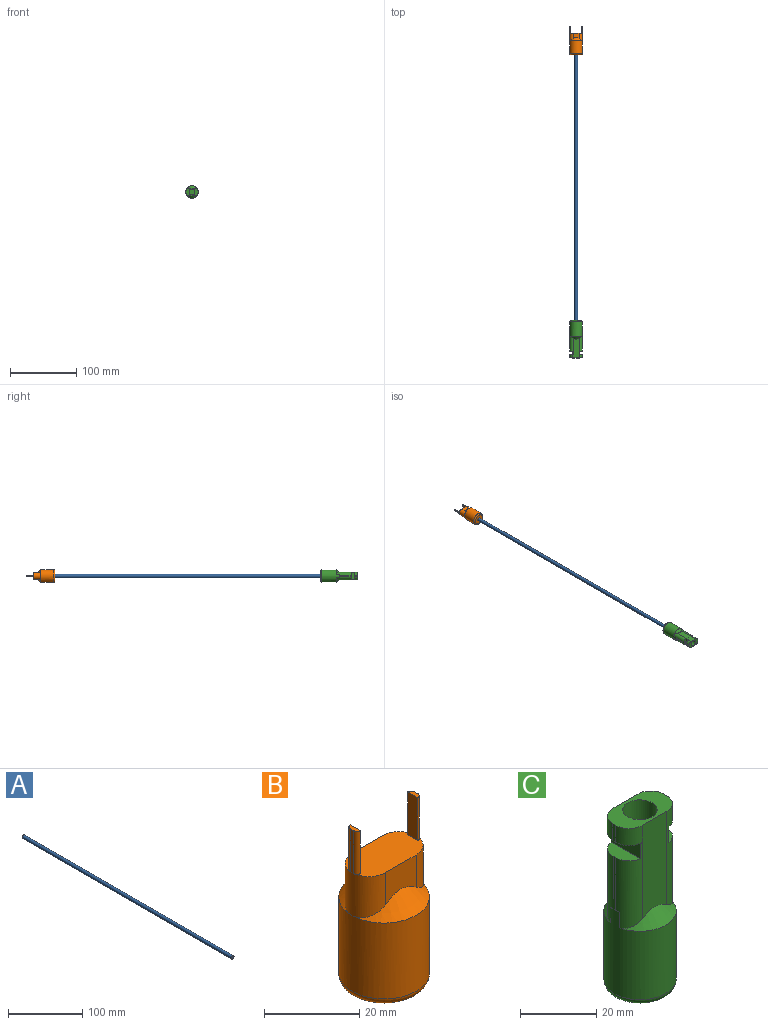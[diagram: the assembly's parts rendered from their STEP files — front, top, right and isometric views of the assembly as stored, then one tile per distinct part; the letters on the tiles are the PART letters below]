
ASSEMBLY  parts=3 mates=2
PART A: 3 faces, bbox 5x400x5 mm
  f0: cylinder r=2.5mm len=400mm, axis (0,1,0), area 6283.2mm2, adj f1,f2
  f1: plane 5x5mm, normal (0,-1,0), area 19.6mm2, adj f0
  f2: plane 5x5mm, normal (0,1,0), area 19.6mm2, adj f0
PART B: 24 faces, bbox 20.6x20.6x43.5 mm
  f0: plane 18.84x10mm, normal (0,0,1), area 163.5mm2, adj f5,f6,f7,f8,f13,f17,f19,f20
  f1: cone r=4.5mm half-angle=45deg, axis (0,0,-1), area 81.3mm2, adj f3,f6,f7,f8
  f2: plane 15x15mm, normal (0,0,-1), area 176.7mm2, adj f23
  f3: cylinder r=9.5mm len=19.5mm, axis (0,0,1), area 1164mm2, adj f1,f4,f23
  f4: cone r=4.5mm half-angle=45deg, axis (0,0,-1), area 81.3mm2, adj f3,f5,f7,f8
  f5: plane 9.01x8.23mm, normal (0,-1,0), area 64mm2, adj f0,f4,f7,f8
  f6: plane 9.01x8.23mm, normal (0,1,0), area 64mm2, adj f0,f1,f7,f8
  f7: cylinder r=5mm len=11mm, axis (0,0,1), area 158mm2, adj f0,f1,f4,f5,f6,f14,f15
  f8: cylinder r=5mm len=11mm, axis (0,0,-1), area 158mm2, adj f0,f1,f4,f5,f6,f9,f10
  f9: plane 0.89x0.08mm, normal (0,0,-1), area 0mm2, adj f8,f11,f20
  f10: plane 0.89x0.08mm, normal (0,0,-1), area 0mm2, adj f8,f11,f19
  f11: plane 11x1mm, normal (1,0,0), area 11mm2, adj f9,f10,f12,f19,f20
  f12: plane 3x1mm, normal (0,0,1), area 2.6mm2, adj f11,f13,f19,f20
  f13: plane 11x3mm, normal (-1,0,0), area 33mm2, adj f0,f12,f19,f20
  f14: plane 0.89x0.08mm, normal (0,0,-1), area 0mm2, adj f7,f16,f21
  f15: plane 0.89x0.08mm, normal (0,0,-1), area 0mm2, adj f7,f16,f22
  f16: plane 11x1mm, normal (-1,0,0), area 11mm2, adj f14,f15,f18,f21,f22
  f17: plane 11x3mm, normal (1,0,0), area 33mm2, adj f0,f18,f21,f22
  f18: plane 3x1mm, normal (0,0,1), area 2.6mm2, adj f16,f17,f21,f22
  f19: cylinder r=1mm len=11mm, axis (0,0,1), area 17.3mm2, adj f0,f10,f11,f12,f13
  f20: cylinder r=1mm len=11mm, axis (0,0,-1), area 17.3mm2, adj f0,f9,f11,f12,f13
  f21: cylinder r=1mm len=11mm, axis (0,0,-1), area 17.3mm2, adj f0,f14,f16,f17,f18
  f22: cylinder r=1mm len=11mm, axis (0,0,1), area 17.3mm2, adj f0,f15,f16,f17,f18
  f23: torus R=7.5mm, axis (0,0,1), area 173.2mm2, adj f2,f3
PART C: 30 faces, bbox 20.6x20.6x56.5 mm
  f0: cylinder r=9.5mm len=27.03mm, axis (0,0,1), area 1351.2mm2, adj f2,f3,f4,f5,f19,f20,f21,f22
  f1: plane 15x15mm, normal (0,0,-1), area 176.7mm2, adj f29
  f2: plane 1.8x0.17mm, normal (0,0,-1), area 0mm2, adj f0,f9,f21
  f3: plane 1.8x0.17mm, normal (0,0,-1), area 0mm2, adj f0,f9,f23
  f4: plane 1.8x0.17mm, normal (0,0,-1), area 0mm2, adj f0,f8,f22
  f5: plane 1.8x0.17mm, normal (0,0,-1), area 0mm2, adj f0,f8,f24
  f6: plane 10.87x5mm, normal (-1,0,0), area 54.4mm2, adj f7,f16,f22,f24
  f7: plane 10.87x4.2mm, normal (0,0,1), area 35.5mm2, adj f6,f8,f22,f24
  f8: plane 16.97x1mm, normal (-1,0,0), area 17mm2, adj f4,f5,f7,f22,f24
  f9: plane 16.97x1mm, normal (1,0,0), area 17mm2, adj f2,f3,f10,f21,f23
  f10: plane 10.87x4.2mm, normal (0,0,1), area 35.5mm2, adj f9,f11,f21,f23
  f11: plane 10.87x5mm, normal (1,0,0), area 54.4mm2, adj f10,f12,f21,f23
  f12: plane 10.87x4.16mm, normal (0,0,-1), area 35.4mm2, adj f11,f13,f21,f23
  f13: plane 5.46x2.29mm, normal (1,0,0), area 12.5mm2, adj f12,f14,f21,f23
  f14: plane 19x11mm, normal (0,0,1), area 124.1mm2, adj f13,f15,f17,f18,f21,f23,f25,f26
  f15: plane 5.46x1mm, normal (-1,0,0), area 5.5mm2, adj f14,f16,f25,f26
  f16: plane 11x5.04mm, normal (0,0,-1), area 36mm2, adj f6,f15,f17,f18,f22,f24,f25,f26
  f17: plane 30.04x9.05mm, normal (0,-1,0), area 261.2mm2, adj f14,f16,f20,f23,f24,f26
  f18: plane 30.04x9.05mm, normal (0,1,0), area 261.2mm2, adj f14,f16,f19,f21,f22,f25
  f19: cone r=9.5mm half-angle=45deg, axis (0,0,-1), area 68mm2, adj f0,f18,f21,f22
  f20: cone r=9.5mm half-angle=45deg, axis (0,0,-1), area 68mm2, adj f0,f17,f23,f24
  f21: cylinder r=5mm len=32.43mm, axis (0,0,1), area 203.5mm2, adj f0,f2,f9,f10,f11,f12,f13,f14
  f22: cylinder r=5mm len=26.97mm, axis (0,0,-1), area 164.2mm2, adj f0,f4,f6,f7,f8,f16,f18,f19
  f23: cylinder r=5mm len=32.43mm, axis (0,0,-1), area 203.5mm2, adj f0,f3,f9,f10,f11,f12,f13,f14
  f24: cylinder r=5mm len=26.97mm, axis (0,0,1), area 164.2mm2, adj f0,f5,f6,f7,f8,f16,f17,f20
  f25: cylinder r=5mm len=5.46mm, axis (0,0,-1), area 42.9mm2, adj f14,f15,f16,f18
  f26: cylinder r=5mm len=5.46mm, axis (0,0,1), area 42.9mm2, adj f14,f15,f16,f17
  f27: cylinder r=4.51mm len=10mm, axis (0,0,1), area 283.3mm2, adj f14,f28
  f28: plane 9.02x9.02mm, normal (0,0,1), area 63.9mm2, adj f27
  f29: torus R=7.5mm, axis (0,0,1), area 173.2mm2, adj f0,f1
PLACE A t=(-389.08,66.26,-41.09)mm
PLACE B rot(axis=(-1,0,0),90deg) t=(-352.89,224.95,-9.02)mm
PLACE C rot(axis=(1,0,0),90deg) t=(-432.11,-468.43,-9.02)mm
MATE fastened C.f0 <-> A.f0  axis (0,1,0) through (16.93,-333.74,-9.02)mm
MATE fastened B.f1 <-> A.f0  axis (0,-1,0) through (16.93,66.26,-9.02)mm
